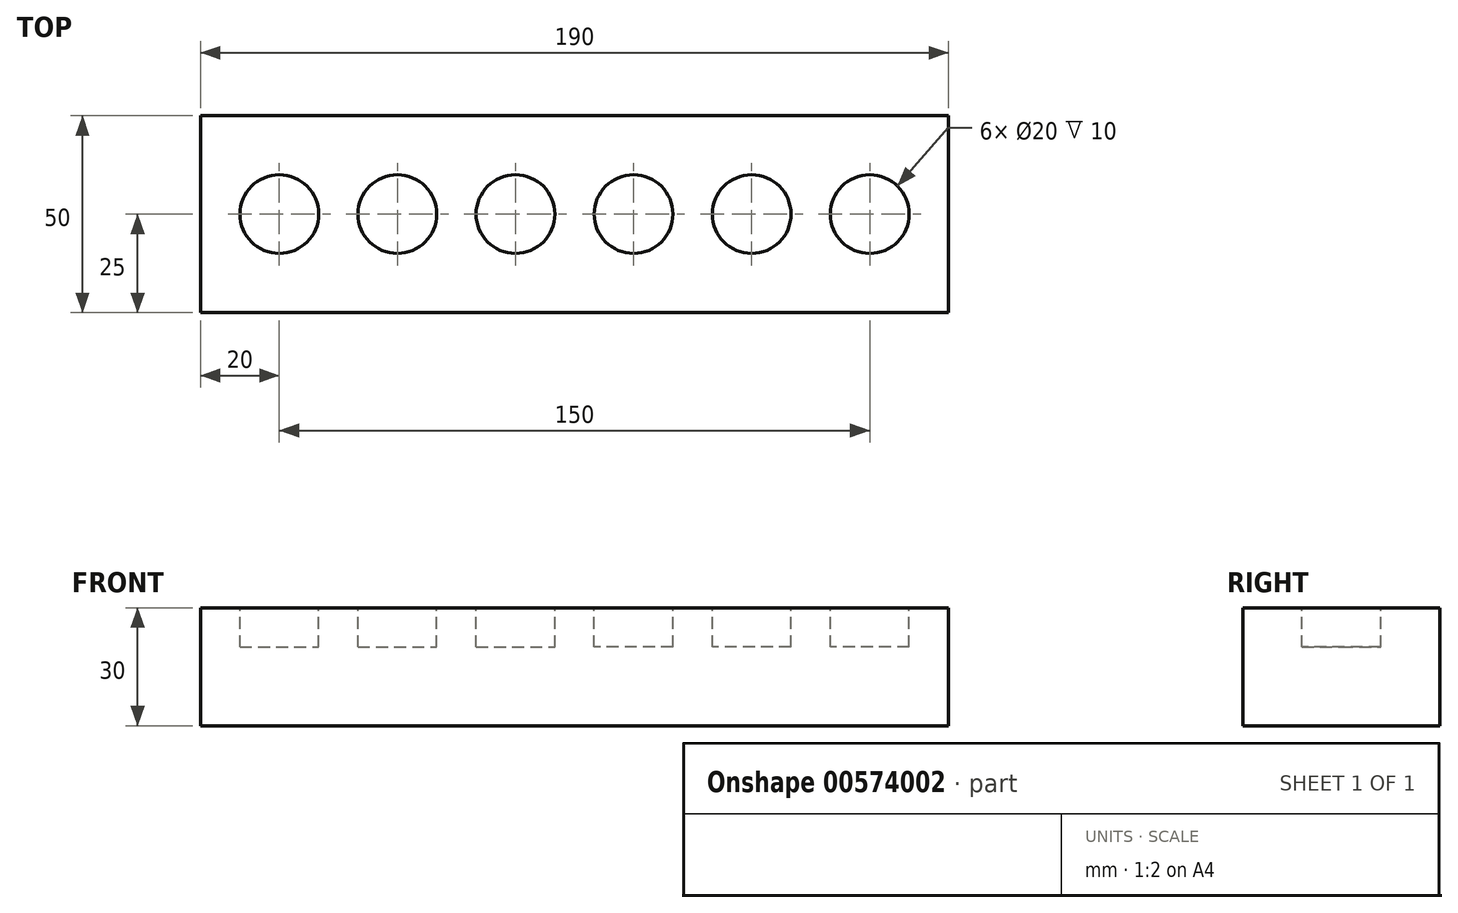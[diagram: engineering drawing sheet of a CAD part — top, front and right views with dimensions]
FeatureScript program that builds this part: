
annotation { "Feature Type Name" : "Feature", "Feature Type Description" : "" }
export const myFeature = defineFeature(function(context is Context, id is Id, definition is map)
    precondition{}
    {
        {
            var Q0;
            Q0=qCreatedBy(makeId("Top.planeOp"),FACE);
            var sketch = newSketch(context, id + "F0", { "sketchPlane" : qUnion([Q0])});
            skLineSegment(sketch, "E0.bottom", {"start": v(0, -25) * mm, "end": v(95, -25) * mm});
            skLineSegment(sketch, "E0.top", {"start": v(0, 25) * mm, "end": v(95, 25) * mm});
            skLineSegment(sketch, "E0.left", {"start": v(0, -25) * mm, "end": v(0, 25) * mm});
            skLineSegment(sketch, "E0.right", {"start": v(95, -25) * mm, "end": v(95, 25) * mm});
            skSolve(sketch);
        }
        {
            var Q0;
            Q0 = qSketchRegion(id + "F0", true);
            extrude(context, id + "F1", {"entities" : qUnion([Q0]), "depth" : 30 * mm, "offsetDistance" : 25 * mm});
        }
        {
            var Q0;
            Q0=makeQuery(id+"F1.opExtrude","CAP_FACE",FACE,{"disambiguationData":[OSD([sQuery(id+"F0.wireOp",EDGE,"E0.bottom"),sQuery(id+"F0.wireOp",EDGE,"E0.top"),sQuery(id+"F0.wireOp",EDGE,"E0.left"),sQuery(id+"F0.wireOp",EDGE,"E0.right")])],"isStart":false});
            var sketch = newSketch(context, id + "F2", { "sketchPlane" : qUnion([Q0])});
            skCircle(sketch, "E1", {"center": v(15, 0) * mm, "radius": 10 * mm});
            skCircle(sketch, "E2", {"center": v(45, 0) * mm, "radius": 10 * mm});
            skCircle(sketch, "E3", {"center": v(75, 0) * mm, "radius": 10 * mm});
            skSolve(sketch);
        }
        {
            var Q0;
            Q0 = qSketchRegion(id + "F2", true);
            extrude(context, id + "F3", {"entities" : qUnion([Q0]), "operationType" : NewBodyOperationType.REMOVE, "oppositeDirection" : true, "depth" : 10 * mm, "offsetDistance" : 25 * mm});
        }
        {
            var Q0;
            Q0=makeQuery(id+"F1.opExtrude","SWEPT_BODY",BODY,{"disambiguationData":[OSD([sQuery(id+"F0.wireOp",EDGE,"E0.bottom"),sQuery(id+"F0.wireOp",EDGE,"E0.top"),sQuery(id+"F0.wireOp",EDGE,"E0.left"),sQuery(id+"F0.wireOp",EDGE,"E0.right")])]});
            var Q1;
            Q1=makeQuery(id+"F1.opExtrude","SWEPT_FACE",FACE,{"disambiguationData":[OSD([sQuery(id+"F0.wireOp",EDGE,"E0.left")])]});
            mirror(context, id + "F4", {"operationType" : NewBodyOperationType.ADD, "entities" : qUnion([Q0]), "mirrorPlane" : qUnion([Q1])});
        }
    });
